# Revit family: ISI_IdealStandard_BathTaps_Melange_A6120
name_source: partatom
category: Plumbing Fixtures
revit_build: Autodesk Revit MEP 2012 (Build: 20110309_2315(x64)
units: mm (PartAtom-declared; Revit-internal decimal feet)

## types (1)
- A6120AA - Melange Freestanding bath shower mixer
    Accessories = www.idealspec.co.uk
    AreaUnits = millimeters
    Assembly Code = C1030200
    AssetType = Fixed
    BIMObjectName = ASH_ArmitageShanks_MixerTaps_Melange-Freestandingbathmxr_A6120
    BREEAMApproved = No
    Brand = Ideal Standard
    CWFU = 0
    Color = Chrome
    ConnectionType = Plumbing
    Cost = 0 $
    Default Elevation = 1219 mm
    Description = Melange freestanding bath shower mixer. Requires Mounting Kit A6133NU.
    DurationUnit = year
    ECA = No
    ExpectedLife = 30
    FaucetFunction = MIXED
    FaucetOperation = OTHER
    FaucetType = OTHER
    Features = Freestanding bath shower mixer with detachable handset. 27 L/min flow rate
    Finish = Chrome
    HWFU = 0
    IfcExportAs = IfcValveType
    IfcExportType = FAUCET
    InstallationInstructions = www.idealspec.co.uk/resources.html
    LinearUnits = millimeters
    ManufacturerURL = www.idealspec.co.uk
    Material = Brass
    Model = A6120AA & A6133NU
    ModelNumber = A6120AA & A6133NU
    ModelReference = Melange freestanding bath shower mixer
    NBSDescription = Water supply fittings for baths
    NBSReference = 45-35-70/315
    Name = MixerTaps_Melange-Freestandingbathmxr-A6120_IdealStandard
    NettWeight = 7 Kg
    NominalHeight = 913 mm
    NominalLength = 338 mm
    NominalWidth = 179 mm
    ProductInformation = www.idealspec.co.uk/assets/datasheet/A6120AA
    Shape = Sculptured
    Space = Internal
    SpareParts = www.fastpart-spares.co.uk
    TestPressure = 10 Bar
    URL = www.idealspec.co.uk
    Uniclass2 = Pr_40_20_87_09
    ValveOperation = Lever
    Version = 2
    VolumeUnits = Litres
    WFU = 0
    WRAS = No
    WarrantyDescription = Manufacturers Warranty
    WarrantyDurationParts = 5
    WarrantyDurationUnit = year
    WaterEfficientProduct = No
    WorkingPressure = 1-3 Bar (27 L/min @ 3 Bar)

## geometry (parser evidence)
native form markers: Sweep x2
no freeform markers — native parametric forms only
